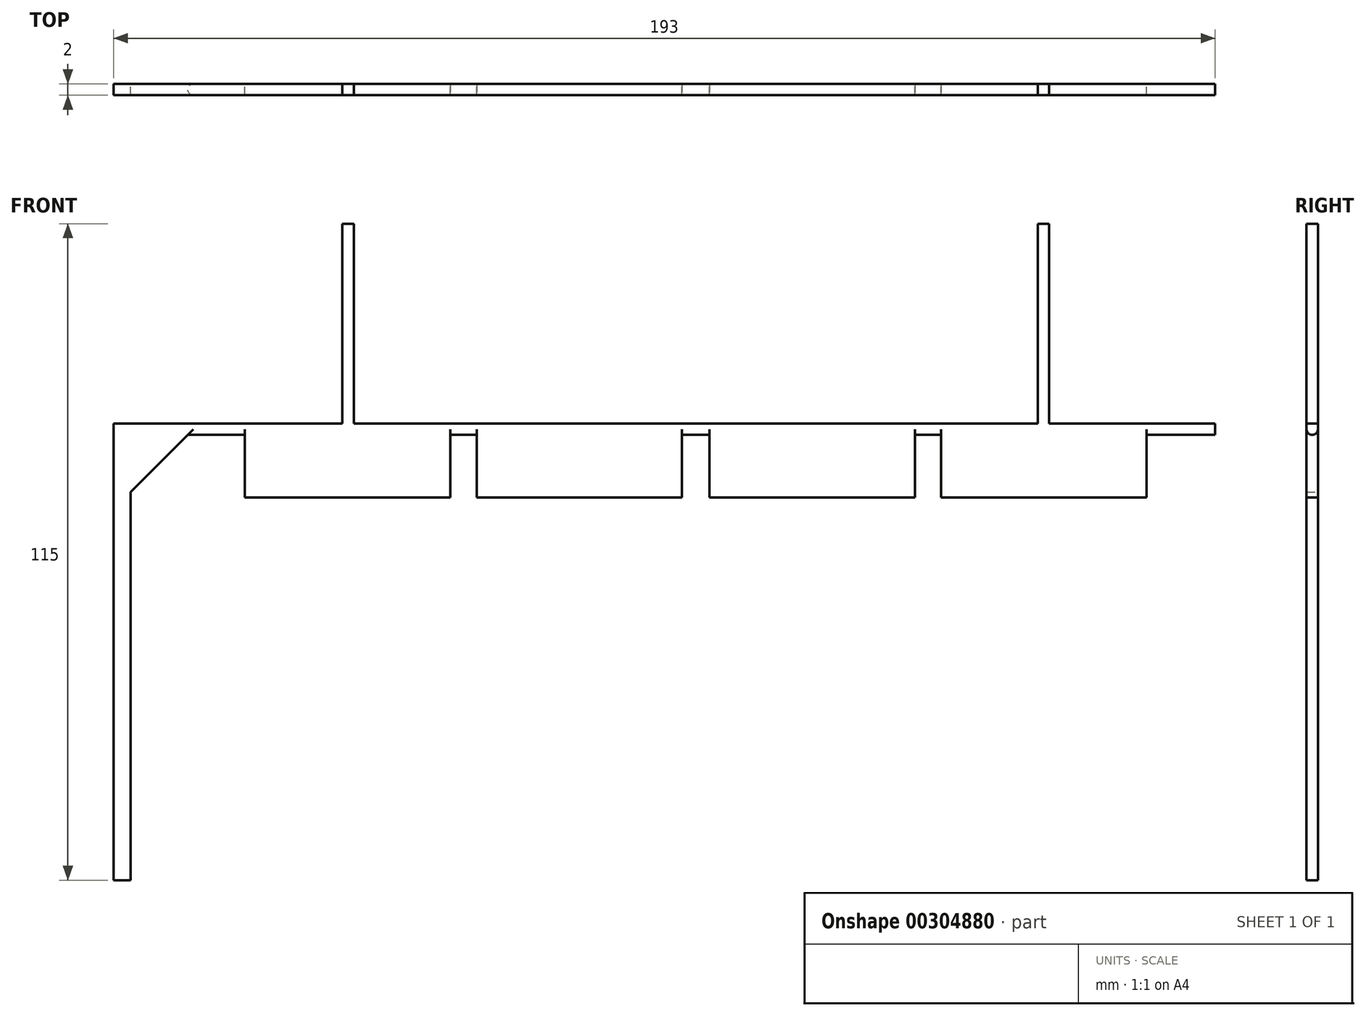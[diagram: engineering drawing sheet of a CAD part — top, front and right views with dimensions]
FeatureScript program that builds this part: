
annotation { "Feature Type Name" : "Feature", "Feature Type Description" : "" }
export const myFeature = defineFeature(function(context is Context, id is Id, definition is map)
    precondition{}
    {
        {
            var Q0;
            Q0=qCreatedBy(makeId("Front.planeOp"),FACE);
            var sketch = newSketch(context, id + "F0", { "sketchPlane" : qUnion([Q0])});
            skLineSegment(sketch, "E0", {"start": v(0, 0) * mm, "end": v(59.9, 0) * mm});
            skLineSegment(sketch, "E1", {"start": v(79, -2) * mm, "end": v(79, -13) * mm});
            skLineSegment(sketch, "E2", {"start": v(79, -13) * mm, "end": v(43, -13) * mm});
            skLineSegment(sketch, "E3", {"start": v(0, -18.13) * mm, "end": v(0, 5.22) * mm, "construction": true});
            skLineSegment(sketch, "E4", {"start": v(43, -13) * mm, "end": v(43, -2) * mm});
            skLineSegment(sketch, "E5", {"start": v(38.4, -13) * mm, "end": v(38.4, -2) * mm});
            skLineSegment(sketch, "E6", {"start": v(2.4, -13) * mm, "end": v(2.4, -2) * mm});
            skLineSegment(sketch, "E7", {"start": v(43, -2) * mm, "end": v(38.4, -2) * mm});
            skLineSegment(sketch, "E8.trimOffspring", {"start": v(38.4, -13) * mm, "end": v(2.4, -13) * mm});
            skPoint(sketch, "E9.orphan", {"position": v(2.2, 0) * mm});
            skPoint(sketch, "E10.start.orphan", {"position": v(0, -13) * mm});
            skLineSegment(sketch, "E11.trimOffspring", {"start": v(2.4, -2) * mm, "end": v(0, -2) * mm});
            skPoint(sketch, "E12.orphan", {"position": v(79, -2) * mm});
            skLineSegment(sketch, "E13", {"start": v(79, 0) * mm, "end": v(91, 0) * mm});
            skLineSegment(sketch, "E14", {"start": v(91, 0) * mm, "end": v(91, -2) * mm});
            skLineSegment(sketch, "E15", {"start": v(91, -2) * mm, "end": v(79, -2) * mm});
            skLineSegment(sketch, "E16.MirrorCS", {"start": v(0, 0) * mm, "end": v(-59.9, 0) * mm});
            skLineSegment(sketch, "E17.MirrorCS", {"start": v(-38.4, -13) * mm, "end": v(-2.4, -13) * mm});
            skLineSegment(sketch, "E18.MirrorCS", {"start": v(-38.4, -13) * mm, "end": v(-38.4, -2) * mm});
            skLineSegment(sketch, "E19.MirrorCS", {"start": v(-43, -2) * mm, "end": v(-38.4, -2) * mm});
            skLineSegment(sketch, "E20.MirrorCS", {"start": v(-43, -13) * mm, "end": v(-43, -2) * mm});
            skLineSegment(sketch, "E21.MirrorCS", {"start": v(-79, -13) * mm, "end": v(-43, -13) * mm});
            skLineSegment(sketch, "E22.MirrorCS", {"start": v(-79, -2) * mm, "end": v(-79, -13) * mm});
            skLineSegment(sketch, "E23.MirrorCS", {"start": v(-2.4, -13) * mm, "end": v(-2.4, -2) * mm});
            skLineSegment(sketch, "E24.MirrorCS", {"start": v(-2.4, -2) * mm, "end": v(0, -2) * mm});
            skLineSegment(sketch, "E25", {"start": v(-79, 0) * mm, "end": v(-100, 0) * mm});
            skLineSegment(sketch, "E26", {"start": v(-89, -2) * mm, "end": v(-79, -2) * mm});
            skPoint(sketch, "E26.endSnap0", {"position": v(-79, -6.5) * mm});
            skLineSegment(sketch, "E27", {"start": v(-99, -12) * mm, "end": v(-99, -80) * mm});
            skLineSegment(sketch, "E28", {"start": v(-99, -80) * mm, "end": v(-102, -80) * mm});
            skLineSegment(sketch, "E29", {"start": v(-102, -80) * mm, "end": v(-102, 0) * mm});
            skLineSegment(sketch, "E30", {"start": v(-102, 0) * mm, "end": v(-100, 0) * mm});
            skLineSegment(sketch, "E31", {"start": v(61.9, 0) * mm, "end": v(61.9, 35) * mm});
            skLineSegment(sketch, "E32", {"start": v(61.9, 35) * mm, "end": v(59.9, 35) * mm});
            skLineSegment(sketch, "E33", {"start": v(59.9, 35) * mm, "end": v(59.9, 0) * mm});
            skLineSegment(sketch, "E34.trimOffspring", {"start": v(61.9, 0) * mm, "end": v(79, 0) * mm});
            skLineSegment(sketch, "E35.MirrorCS", {"start": v(-61.9, 0) * mm, "end": v(-61.9, 35) * mm});
            skLineSegment(sketch, "E36.MirrorCS", {"start": v(-59.9, 35) * mm, "end": v(-59.9, 0) * mm});
            skLineSegment(sketch, "E37.MirrorCS", {"start": v(-61.9, 35) * mm, "end": v(-59.9, 35) * mm});
            skLineSegment(sketch, "E38.trimOffspring", {"start": v(-61.9, 0) * mm, "end": v(-79, 0) * mm});
            skPoint(sketch, "E39.orphan", {"position": v(-79, 0) * mm});
            skPoint(sketch, "E40.orphan", {"position": v(-79, -1) * mm});
            skPoint(sketch, "E41.end.orphan", {"position": v(-103.54, -1) * mm});
            skPoint(sketch, "E42.orphan", {"position": v(103.54, -1) * mm});
            skPoint(sketch, "E43.MirrorCS.start.orphan", {"position": v(79, -1) * mm});
            skLineSegment(sketch, "E44", {"start": v(-89, -2) * mm, "end": v(-99, -12) * mm});
            skPoint(sketch, "E45.orphan", {"position": v(-99, -2) * mm});
            skSolve(sketch);
        }
        {
            var Q0;
            Q0=makeQuery(id+"F0.imprint","IMPRINT",FACE,{"disambiguationData":[TD([[makeQuery(id+"F0.imprint","IMPRINT",EDGE,{"derivedFrom":sQuery(id+"F0.wireOp",EDGE,"E0")}),-1.0]])]});
            extrude(context, id + "F1", {"entities" : qUnion([Q0]), "depth" : 2 * mm});
        }
        {
            var Q0;
            Q0=makeQuery(id+"F1.opExtrude","CAP_EDGE",EDGE,{"disambiguationData":[OSD([sQuery(id+"F0.wireOp",EDGE,"E26")])],"isStart":false});
            var Q1;
            Q1=makeQuery(id+"F1.opExtrude","CAP_EDGE",EDGE,{"disambiguationData":[OSD([sQuery(id+"F0.wireOp",EDGE,"E26")])],"isStart":true});
            var Q2;
            Q2=makeQuery(id+"F1.opExtrude","CAP_EDGE",EDGE,{"disambiguationData":[OSD([sQuery(id+"F0.wireOp",EDGE,"E15")])],"isStart":true});
            var Q3;
            Q3=makeQuery(id+"F1.opExtrude","CAP_EDGE",EDGE,{"disambiguationData":[OSD([sQuery(id+"F0.wireOp",EDGE,"E15")])],"isStart":false});
            fillet(context, id + "F2", {"entities" : qUnion([Q0, Q1, Q2, Q3]), "radius" : 1 * mm, "tangentPropagation" : true, "allowEdgeOverflow" : false});
        }
        {
            var Q0;
            Q0=makeQuery(id+"F1.opExtrude","CAP_EDGE",EDGE,{"disambiguationData":[OSD([sQuery(id+"F0.wireOp",EDGE,"E19.MirrorCS")])],"isStart":false});
            var Q1;
            Q1=makeQuery(id+"F1.opExtrude","CAP_EDGE",EDGE,{"disambiguationData":[OSD([sQuery(id+"F0.wireOp",EDGE,"E11.trimOffspring"),sQuery(id+"F0.wireOp",EDGE,"E24.MirrorCS")])],"isStart":false});
            var Q2;
            Q2=makeQuery(id+"F1.opExtrude","CAP_EDGE",EDGE,{"disambiguationData":[OSD([sQuery(id+"F0.wireOp",EDGE,"E7")])],"isStart":false});
            var Q3;
            Q3=makeQuery(id+"F1.opExtrude","CAP_EDGE",EDGE,{"disambiguationData":[OSD([sQuery(id+"F0.wireOp",EDGE,"E19.MirrorCS")])],"isStart":true});
            var Q4;
            Q4=makeQuery(id+"F1.opExtrude","CAP_EDGE",EDGE,{"disambiguationData":[OSD([sQuery(id+"F0.wireOp",EDGE,"E11.trimOffspring"),sQuery(id+"F0.wireOp",EDGE,"E24.MirrorCS")])],"isStart":true});
            var Q5;
            Q5=makeQuery(id+"F1.opExtrude","CAP_EDGE",EDGE,{"disambiguationData":[OSD([sQuery(id+"F0.wireOp",EDGE,"E7")])],"isStart":true});
            fillet(context, id + "F3", {"entities" : qUnion([Q0, Q1, Q2, Q3, Q4, Q5]), "radius" : 1 * mm, "tangentPropagation" : true, "allowEdgeOverflow" : false});
        }
    });
